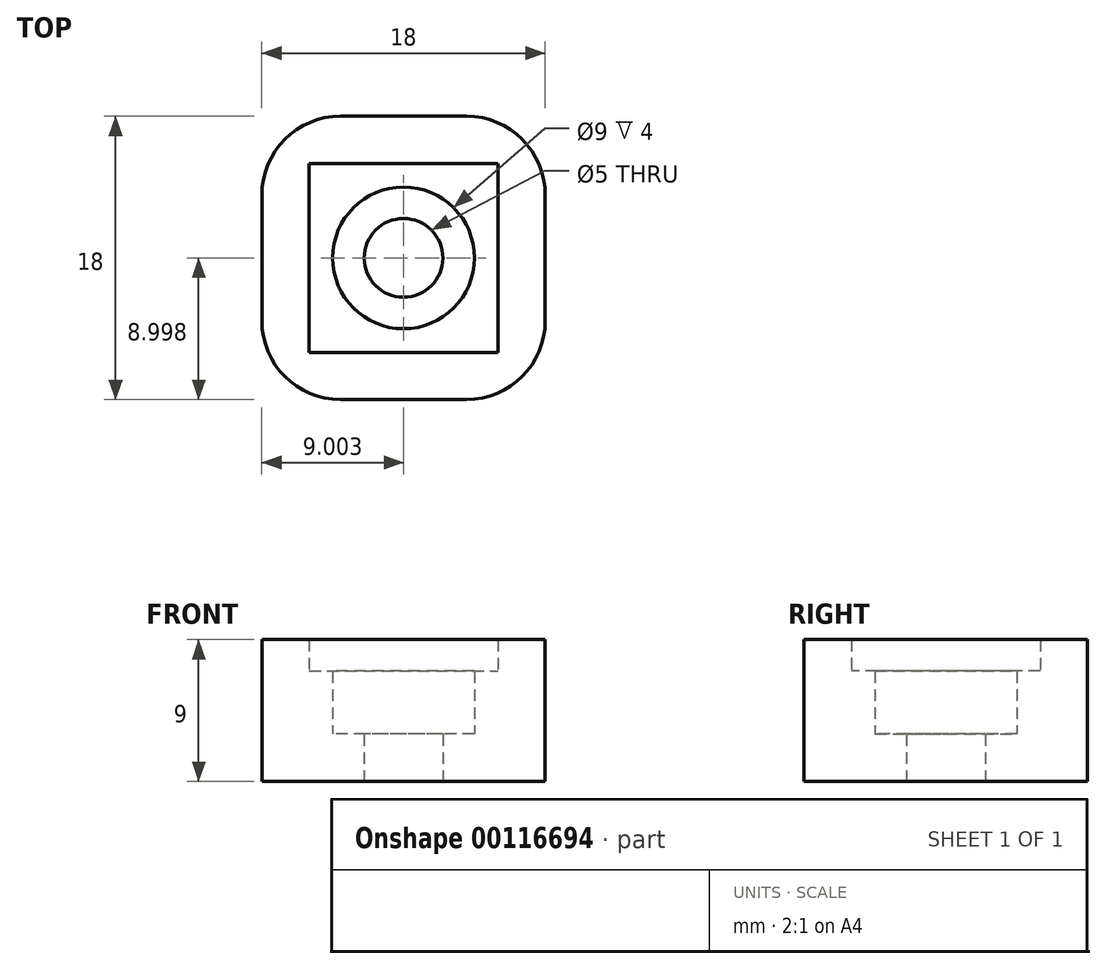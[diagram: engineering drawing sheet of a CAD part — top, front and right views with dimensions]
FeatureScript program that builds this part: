
annotation { "Feature Type Name" : "Feature", "Feature Type Description" : "" }
export const myFeature = defineFeature(function(context is Context, id is Id, definition is map)
    precondition{}
    {
        {
            var Q0;
            Q0=qCreatedBy(makeId("Top.planeOp"),FACE);
            var sketch = newSketch(context, id + "F0", { "sketchPlane" : qUnion([Q0])});
            skLineSegment(sketch, "E0.bottom", {"start": v(-13.24, 7.72) * mm, "end": v(4.76, 7.72) * mm});
            skLineSegment(sketch, "E0.top", {"start": v(-13.24, -10.28) * mm, "end": v(4.76, -10.28) * mm});
            skLineSegment(sketch, "E0.left", {"start": v(-13.24, 7.72) * mm, "end": v(-13.24, -10.28) * mm});
            skLineSegment(sketch, "E0.right", {"start": v(4.76, 7.72) * mm, "end": v(4.76, -10.28) * mm});
            skLineSegment(sketch, "E1.bottom", {"start": v(-10.24, 4.72) * mm, "end": v(1.76, 4.72) * mm});
            skLineSegment(sketch, "E1.top", {"start": v(-10.24, -7.28) * mm, "end": v(1.76, -7.28) * mm});
            skLineSegment(sketch, "E1.left", {"start": v(-10.24, 4.72) * mm, "end": v(-10.24, -7.28) * mm});
            skLineSegment(sketch, "E1.right", {"start": v(1.76, 4.72) * mm, "end": v(1.76, -7.28) * mm});
            skCircle(sketch, "E2", {"center": v(-4.24, -1.28) * mm, "radius": 2.5 * mm});
            skCircle(sketch, "E3", {"center": v(-4.24, -1.28) * mm, "radius": 4.5 * mm});
            skSolve(sketch);
        }
        {
            var Q0;
            Q0=makeQuery(id+"F0.imprint","IMPRINT",FACE,{"disambiguationData":[TD([[makeQuery(id+"F0.imprint","IMPRINT",EDGE,{"derivedFrom":sQuery(id+"F0.wireOp",EDGE,"E1.bottom")}),-1.0]])]});
            extrude(context, id + "F1", {"entities" : qUnion([Q0]), "depth" : 7 * mm});
        }
        {
            var Q0;
            Q0 = qSketchRegion(id + "F0", true);
            extrude(context, id + "F2", {"entities" : qUnion([Q0]), "operationType" : NewBodyOperationType.ADD, "depth" : 9 * mm});
        }
        {
            var Q0;
            Q0=makeQuery(id+"F2.opExtrude","SWEPT_EDGE",EDGE,{"disambiguationData":[OSD([sQuery(id+"F0.wireOp",EDGE,"E0.top"),sQuery(id+"F0.wireOp",EDGE,"E0.left")])]});
            var Q1;
            Q1=makeQuery(id+"F2.opExtrude","SWEPT_EDGE",EDGE,{"disambiguationData":[OSD([sQuery(id+"F0.wireOp",EDGE,"E0.top"),sQuery(id+"F0.wireOp",EDGE,"E0.right")])]});
            var Q2;
            Q2=makeQuery(id+"F2.opExtrude","SWEPT_EDGE",EDGE,{"disambiguationData":[OSD([sQuery(id+"F0.wireOp",EDGE,"E0.bottom"),sQuery(id+"F0.wireOp",EDGE,"E0.right")])]});
            var Q3;
            Q3=makeQuery(id+"F2.opExtrude","SWEPT_EDGE",EDGE,{"disambiguationData":[OSD([sQuery(id+"F0.wireOp",EDGE,"E0.bottom"),sQuery(id+"F0.wireOp",EDGE,"E0.left")])]});
            fillet(context, id + "F3", {"entities" : qUnion([Q0, Q1, Q2, Q3]), "radius" : 5 * mm, "tangentPropagation" : true, "allowEdgeOverflow" : false});
        }
        {
            var Q0;
            Q0=makeQuery(id+"F0.imprint","IMPRINT",FACE,{"disambiguationData":[TD([[makeQuery(id+"F0.imprint","IMPRINT",EDGE,{"derivedFrom":sQuery(id+"F0.wireOp",EDGE,"E2")}),-1.0]])]});
            extrude(context, id + "F4", {"entities" : qUnion([Q0]), "operationType" : NewBodyOperationType.ADD, "depth" : 3 * mm});
        }
    });
